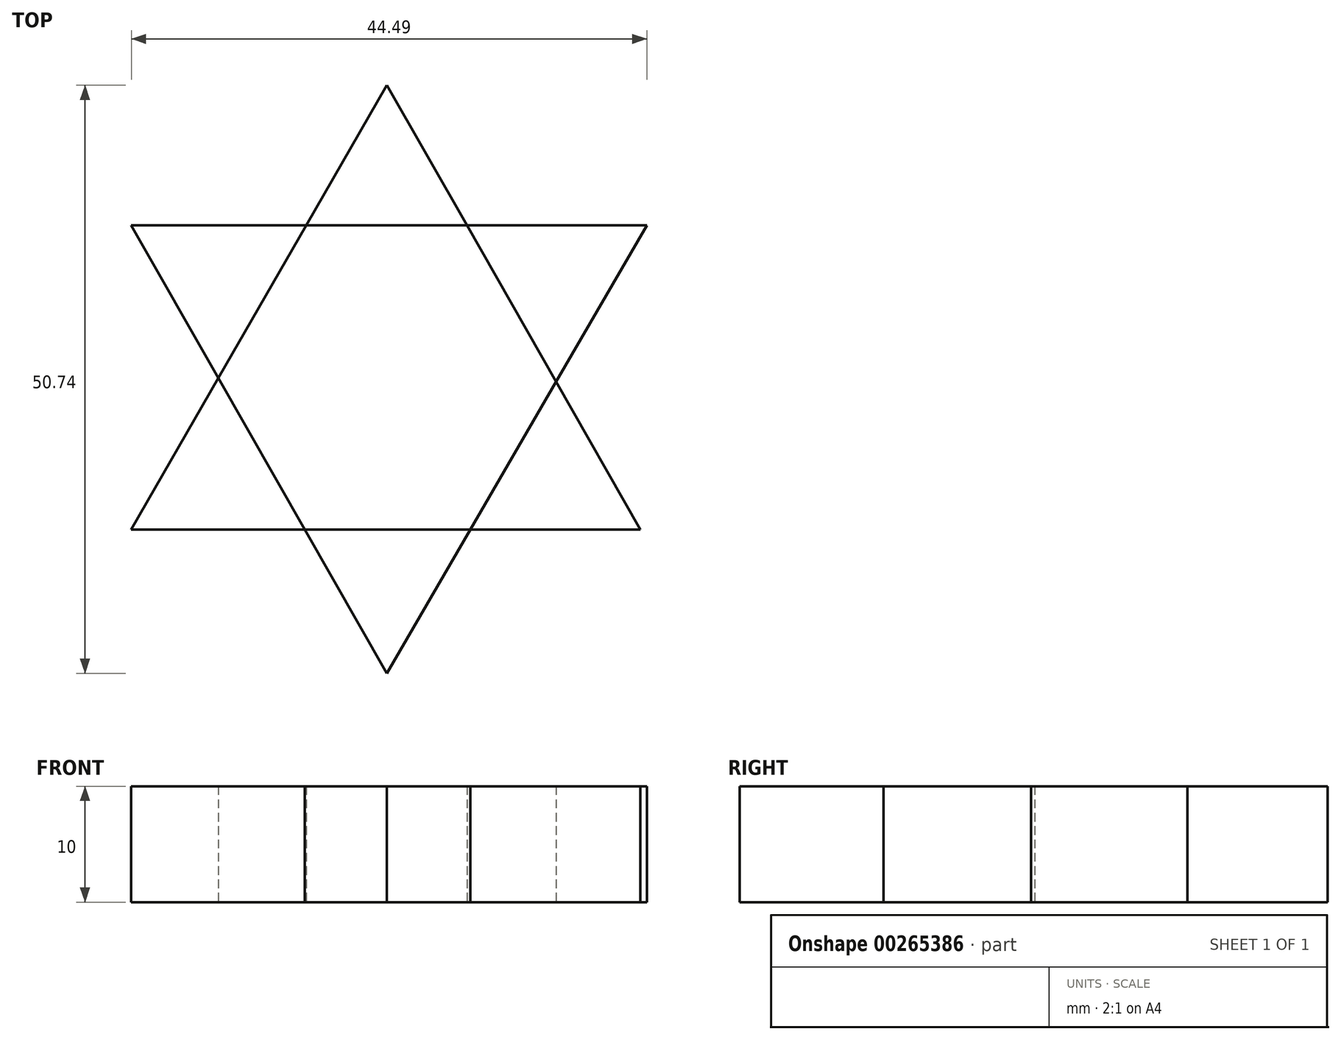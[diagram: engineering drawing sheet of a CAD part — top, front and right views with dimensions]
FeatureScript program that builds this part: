
annotation { "Feature Type Name" : "Feature", "Feature Type Description" : "" }
export const myFeature = defineFeature(function(context is Context, id is Id, definition is map)
    precondition{}
    {
        {
            var Q0;
            Q0=qCreatedBy(makeId("Top.planeOp"),FACE);
            var sketch = newSketch(context, id + "F0", { "sketchPlane" : qUnion([Q0])});
            skCircle(sketch, "E0.cCircle", {"center": v(0, 0) * mm, "radius": 25.48 * mm, "construction": true});
            skLineSegment(sketch, "E0.0", {"start": v(21.86, -13.09) * mm, "end": v(-0.4, -25.47) * mm});
            skLineSegment(sketch, "E0.1", {"start": v(-0.4, -25.47) * mm, "end": v(-22.27, -12.39) * mm});
            skLineSegment(sketch, "E0.2", {"start": v(-22.27, -12.39) * mm, "end": v(-21.86, 13.09) * mm});
            skLineSegment(sketch, "E0.3", {"start": v(-21.86, 13.09) * mm, "end": v(0.4, 25.47) * mm});
            skLineSegment(sketch, "E0.4", {"start": v(0.4, 25.47) * mm, "end": v(22.27, 12.39) * mm});
            skLineSegment(sketch, "E0.5", {"start": v(22.27, 12.39) * mm, "end": v(21.86, -13.09) * mm});
            skSolve(sketch);
        }
        {
            var Q0;
            Q0=qCreatedBy(makeId("Top.planeOp"),FACE);
            var sketch = newSketch(context, id + "F1", { "sketchPlane" : qUnion([Q0])});
            skLineSegment(sketch, "E1", {"start": v(-22.05, 13.06) * mm, "end": v(22.44, 13.06) * mm});
            skLineSegment(sketch, "E2", {"start": v(22.44, 13.06) * mm, "end": v(0, -25.58) * mm});
            skLineSegment(sketch, "E3", {"start": v(0, -25.58) * mm, "end": v(-22.05, 13.06) * mm});
            skLineSegment(sketch, "E4", {"start": v(0, 25.16) * mm, "end": v(21.87, -13.16) * mm});
            skLineSegment(sketch, "E5", {"start": v(21.87, -13.16) * mm, "end": v(-22.05, -13.16) * mm});
            skLineSegment(sketch, "E6", {"start": v(-22.05, -13.16) * mm, "end": v(0, 25.16) * mm});
            skSolve(sketch);
        }
        {
            var Q0;
            Q0=qCreatedBy(makeId("Top.planeOp"),FACE);
            var sketch = newSketch(context, id + "F2", { "sketchPlane" : qUnion([Q0])});
            skLineSegment(sketch, "E7", {"start": v(-6.83, 12.87) * mm, "end": v(0, 9.55) * mm});
            skLineSegment(sketch, "E8", {"start": v(0, 9.55) * mm, "end": v(6.83, 12.67) * mm});
            skLineSegment(sketch, "E9", {"start": v(6.83, 12.67) * mm, "end": v(6.83, 4.87) * mm});
            skLineSegment(sketch, "E10", {"start": v(6.83, 4.87) * mm, "end": v(14.44, 0) * mm});
            skLineSegment(sketch, "E11", {"start": v(14.44, 0) * mm, "end": v(8.2, -4.11) * mm});
            skLineSegment(sketch, "E12", {"start": v(8.2, -4.11) * mm, "end": v(8.2, -13.28) * mm});
            skLineSegment(sketch, "E13", {"start": v(8.2, -13.28) * mm, "end": v(0, -9) * mm});
            skLineSegment(sketch, "E14", {"start": v(0, -9) * mm, "end": v(-6.64, -13.48) * mm});
            skLineSegment(sketch, "E15", {"start": v(-6.64, -13.48) * mm, "end": v(-6.64, -4.3) * mm});
            skLineSegment(sketch, "E16", {"start": v(-6.64, -4.3) * mm, "end": v(-14.64, 0) * mm});
            skLineSegment(sketch, "E17", {"start": v(-14.64, 0) * mm, "end": v(-7.42, 3.9) * mm});
            skLineSegment(sketch, "E18", {"start": v(-6.83, 12.87) * mm, "end": v(-7.42, 3.9) * mm});
            skSolve(sketch);
        }
        {
            var Q0;
            Q0=sQuery(id+"F0.wireOp",EDGE,"E0.4");
            var Q1;
            Q1=sQuery(id+"F0.wireOp",EDGE,"E0.3");
            var Q2;
            Q2=sQuery(id+"F0.wireOp",EDGE,"E0.2");
            var Q3;
            Q3=sQuery(id+"F0.wireOp",EDGE,"E0.1");
            var Q4;
            Q4=sQuery(id+"F0.wireOp",EDGE,"E0.0");
            var Q5;
            Q5=sQuery(id+"F0.wireOp",EDGE,"E0.5");
            extrude(context, id + "F3", {"bodyType" : ToolBodyType.SURFACE, "surfaceEntities" : qUnion([Q0, Q1, Q2, Q3, Q4, Q5]), "depth" : 10 * mm});
        }
        {
            var Q0;
            Q0=sQuery(id+"F2.wireOp",EDGE,"E12");
            var Q1;
            Q1=sQuery(id+"F2.wireOp",EDGE,"E11");
            var Q2;
            Q2=sQuery(id+"F2.wireOp",EDGE,"E10");
            var Q3;
            Q3=sQuery(id+"F2.wireOp",EDGE,"E9");
            var Q4;
            Q4=sQuery(id+"F2.wireOp",EDGE,"E8");
            var Q5;
            Q5=sQuery(id+"F2.wireOp",EDGE,"E7");
            var Q6;
            Q6=sQuery(id+"F2.wireOp",EDGE,"E18");
            var Q7;
            Q7=sQuery(id+"F2.wireOp",EDGE,"E17");
            var Q8;
            Q8=sQuery(id+"F2.wireOp",EDGE,"E16");
            var Q9;
            Q9=sQuery(id+"F2.wireOp",EDGE,"E15");
            var Q10;
            Q10=sQuery(id+"F2.wireOp",EDGE,"E14");
            var Q11;
            Q11=sQuery(id+"F2.wireOp",EDGE,"E13");
            extrude(context, id + "F4", {"bodyType" : ToolBodyType.SURFACE, "surfaceEntities" : qUnion([Q0, Q1, Q2, Q3, Q4, Q5, Q6, Q7, Q8, Q9, Q10, Q11]), "depth" : 10 * mm});
        }
        {
            var Q0;
            {var subQ0=sQuery(id+"F1.wireOp",EDGE,"E3");var subQ1=sQuery(id+"F1.wireOp",EDGE,"E1");var subQ2=makeQuery(id+"F1.imprint","INTERSECT",VERTEX,{"derivedFrom":[subQ1,subQ0]});Q0=makeQuery(id+"F1.imprint","IMPRINT",FACE,{"disambiguationData":[TD([[makeQuery(id+"F1.imprint","IMPRINT",EDGE,{"disambiguationData":[TD([[subQ2,-1.0]])],"derivedFrom":subQ1}),-1.0]])]});}
            var Q1;
            {var subQ0=sQuery(id+"F1.wireOp",EDGE,"E6");var subQ1=sQuery(id+"F1.wireOp",EDGE,"E1");var subQ2=makeQuery(id+"F1.imprint","INTERSECT",VERTEX,{"derivedFrom":[subQ1,subQ0]});Q1=makeQuery(id+"F1.imprint","IMPRINT",FACE,{"disambiguationData":[TD([[makeQuery(id+"F1.imprint","IMPRINT",EDGE,{"disambiguationData":[TD([[subQ2,-1.0]])],"derivedFrom":subQ1}),1.0]])]});}
            var Q2;
            {var subQ0=sQuery(id+"F1.wireOp",EDGE,"E2");var subQ1=sQuery(id+"F1.wireOp",EDGE,"E1");var subQ2=makeQuery(id+"F1.imprint","INTERSECT",VERTEX,{"derivedFrom":[subQ1,subQ0]});Q2=makeQuery(id+"F1.imprint","IMPRINT",FACE,{"disambiguationData":[TD([[makeQuery(id+"F1.imprint","IMPRINT",EDGE,{"disambiguationData":[TD([[subQ2,1.0]])],"derivedFrom":subQ1}),-1.0]])]});}
            var Q3;
            {var subQ0=sQuery(id+"F1.wireOp",EDGE,"E4");var subQ1=sQuery(id+"F1.wireOp",EDGE,"E2");var subQ2=makeQuery(id+"F1.imprint","INTERSECT",VERTEX,{"derivedFrom":[subQ1,subQ0]});Q3=makeQuery(id+"F1.imprint","IMPRINT",FACE,{"disambiguationData":[TD([[makeQuery(id+"F1.imprint","IMPRINT",EDGE,{"disambiguationData":[TD([[subQ2,-1.0]])],"derivedFrom":subQ1}),1.0]])]});}
            var Q4;
            {var subQ0=sQuery(id+"F1.wireOp",EDGE,"E3");var subQ1=sQuery(id+"F1.wireOp",EDGE,"E2");var subQ2=makeQuery(id+"F1.imprint","INTERSECT",VERTEX,{"derivedFrom":[subQ1,subQ0]});Q4=makeQuery(id+"F1.imprint","IMPRINT",FACE,{"disambiguationData":[TD([[makeQuery(id+"F1.imprint","IMPRINT",EDGE,{"disambiguationData":[TD([[subQ2,1.0]])],"derivedFrom":subQ1}),-1.0]])]});}
            var Q5;
            {var subQ0=sQuery(id+"F1.wireOp",EDGE,"E5");var subQ1=sQuery(id+"F1.wireOp",EDGE,"E3");var subQ2=makeQuery(id+"F1.imprint","INTERSECT",VERTEX,{"derivedFrom":[subQ1,subQ0]});Q5=makeQuery(id+"F1.imprint","IMPRINT",FACE,{"disambiguationData":[TD([[makeQuery(id+"F1.imprint","IMPRINT",EDGE,{"disambiguationData":[TD([[subQ2,-1.0]])],"derivedFrom":subQ1}),1.0]])]});}
            extrude(context, id + "F5", {"entities" : qUnion([Q0, Q1, Q2, Q3, Q4, Q5]), "depth" : 10 * mm});
        }
    });
